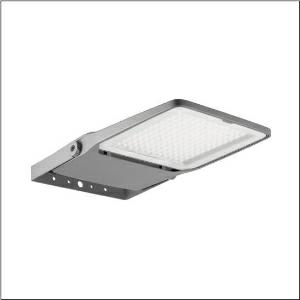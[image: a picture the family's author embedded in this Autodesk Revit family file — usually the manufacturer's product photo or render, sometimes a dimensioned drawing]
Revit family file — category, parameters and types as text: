
# Revit family: floodlight_fl_20_midi___pl43_5xa7682e2a2ac_5f4f
name_source: partatom
category: Lighting Fixtures
units: mm (PartAtom-declared; Revit-internal decimal feet)

## family parameters
Cut with Voids When Loaded = No
Host = Face
Light Source = No
Part Type = Normal
Room Calculation Point = No
Round Connector Dimension = Use Diameter
Shared = No

## types (1)
- --- (1 x LED 4000K / CRI = 70 (unbekannt), 28460 lm, 4000K)
    Apparent Load = 208 VA
    CIE Flux Codes = 32 74 99 100 100
    Color Rendering = 70
    Color Temperature = 4000K
    Default Elevation = 1800 mm
    Description = Floodlight FL 20 midi, floodlight, primary light control with lens, of plastic, primary optical cover: protective disc, of toughened safety glass, transparent, light distribution: PL43, light emission: direct distribution, primary light characteristic: asymmetric, installation type: surface-mounted, LED High Power LED, rated luminous flux: 28.460 lm, light colour: 740, colour temperature: 4000K, control gear: ECG Plus, control: flexible luminous flux parameterisation, time-dependent luminous flux control, digital communication interface, power reduction, overheat protection, electronic power reduction, with terminal, 5-pole, max. 2.5mm², mains connection: 220..240V, AC, 50/60Hz, rated input power: 208W, LED unit, of diecast aluminium, powder-coated, Siteco® metallic grey (DB 702S), length: 731 mm, width: 450 mm, height: 76mm, housing frame, of diecast aluminium, powder-coated, Siteco® metallic grey (DB 702S), wall fastening, of steel, powder-coated, Siteco® metallic grey (DB 702S), DALIprotection rating (complete): IP66, insulation class (complete): insulation class II (safety insulation), certification: CE, ENEC, VDE, protection symbol: D, permissible ambient temperature for indoor applications: -40..+40°C, permissible ambient temperature for outdoor applications: -40..+50°C, standard: DIN EN 12944, packaging unit: 1 piece

Light Distribution: PL43
    Height = 76 mm
    Lamp = 1 x LED 4000K / CRI >= 70 (unbekannt)
    Lamp Light Flux = 28460 lm
    Lamp count = 1
    Length = 731 mm
    Luminous efficacy = 137 lm/W
    Manufacturer = Siteco
    ModVariant = No
    Model = 5XA7682E2A2AC
    Number of Poles = 1
    OnlyDefault = Yes
    Power Factor = 1
    Product Name = Floodlight FL 20 midi | PL43
    Product group = floodlight | pylon top
    ProductGroupID = 6101
    Protection Class = Protection class II
    Protection Degree = IP 66
    RLX_Detail_Level = 1
    RlxData = <blob elided: 91877 chars, md5=d0acaad6>
    Socket = socket
    Standby Power = 0 W
    System Light Flux = 28460 lm
    System Power = 208 W
    Type Comments = factory setting: luminous flux: 100 % | dim-lin: 254 | 484 mA
    Type Image = l_1005944.jpg
    URL = http://relux.com
    VarID = @adj_143657
    Voltage = 0 V
    Weight = 0.00 kg
    Width = 450 mm

## geometry (parser evidence)
native form markers: Blend x4, Sweep x11
no freeform markers — native parametric forms only
